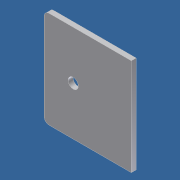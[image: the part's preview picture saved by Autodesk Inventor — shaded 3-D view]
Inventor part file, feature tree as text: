
AUTODESK INVENTOR PART (.ipt)
format: ipt  version: unknown  size: 173,056 bytes
history: native  units: in
note: dims shown in document units (in); Inventor stores cm internally (conversion verified against a paired STEP export)
features: extrude x1, fillet x1, hole x1, sketch x1
ambient origin geometry x8: Origin, YZ Plane, XZ Plane, XY Plane, X Axis, Y Axis, Z Axis, Center Point
bodies: Solid1 (feature_tree)
feature tree (4):
  extrude  "Extrusion1"  Depth=0.125in TaperAngle=0.0deg
  fillet  "Fillet1"  Radius=0.125in
  hole  "Hole1"  [1 undecoded]
  sketch  "Sketch1"  dims[d0=2.25in d1=0.125in d2=0.0in d3=0.125in d4=0.75in d5=1.25in d6=0.265in d7=0.75in d8=0.375in d9=0.25in d10=0.5635in d11=1.0in d12=0.8108in d13=2.5in]
note: 1 required parameter value undecoded (feature->parameter linkage not recoverable at this tier; creation-order binding heuristic only, values carry confidence <= 0.55)
